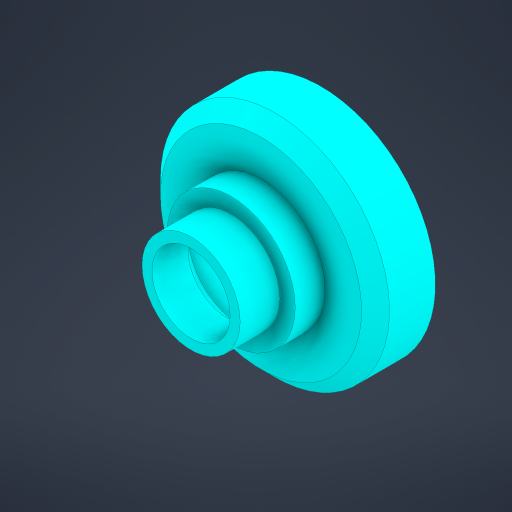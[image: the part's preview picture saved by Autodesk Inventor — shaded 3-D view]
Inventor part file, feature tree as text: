
AUTODESK INVENTOR PART (.ipt)
format: ipt  version: 2023.4 (Build 274418000, 418)  size: 244,224 bytes
history: native  units: mm
features: extrude x5, sketch x1, chamfer x1
ambient origin geometry x8: Origin, YZ Plane, XZ Plane, XY Plane, X Axis, Y Axis, Z Axis, Center Point
bodies: Solid1 (feature_tree)
feature tree (7):
  sketch  "Sketch1"  dims[d0=12.2875mm d1=1.25mm d2=5.0mm d3=0.0mm d4=26.1875mm d5=13.5675mm d6=1.25mm d7=1.25mm d8=1.25mm d9=0.0mm d10=2.5mm d11=0.0mm d12=1.75mm d13=2.0mm d14=45.0deg d15=2.5mm d16=0.0mm d17=5.0mm d18=0.0mm]
  extrude  "Extrusion1"  Depth=1.25mm
  extrude  "Extrusion2"  Depth=5.0mm TaperAngle=0.0deg
  extrude  "Extrusion3"  Depth=5.0mm
  extrude  "Extrusion4"  Depth=5.0mm
  extrude  "Extrusion5"  Depth=1.25mm
  chamfer  "Chamfer1"  Distance=1.25mm
